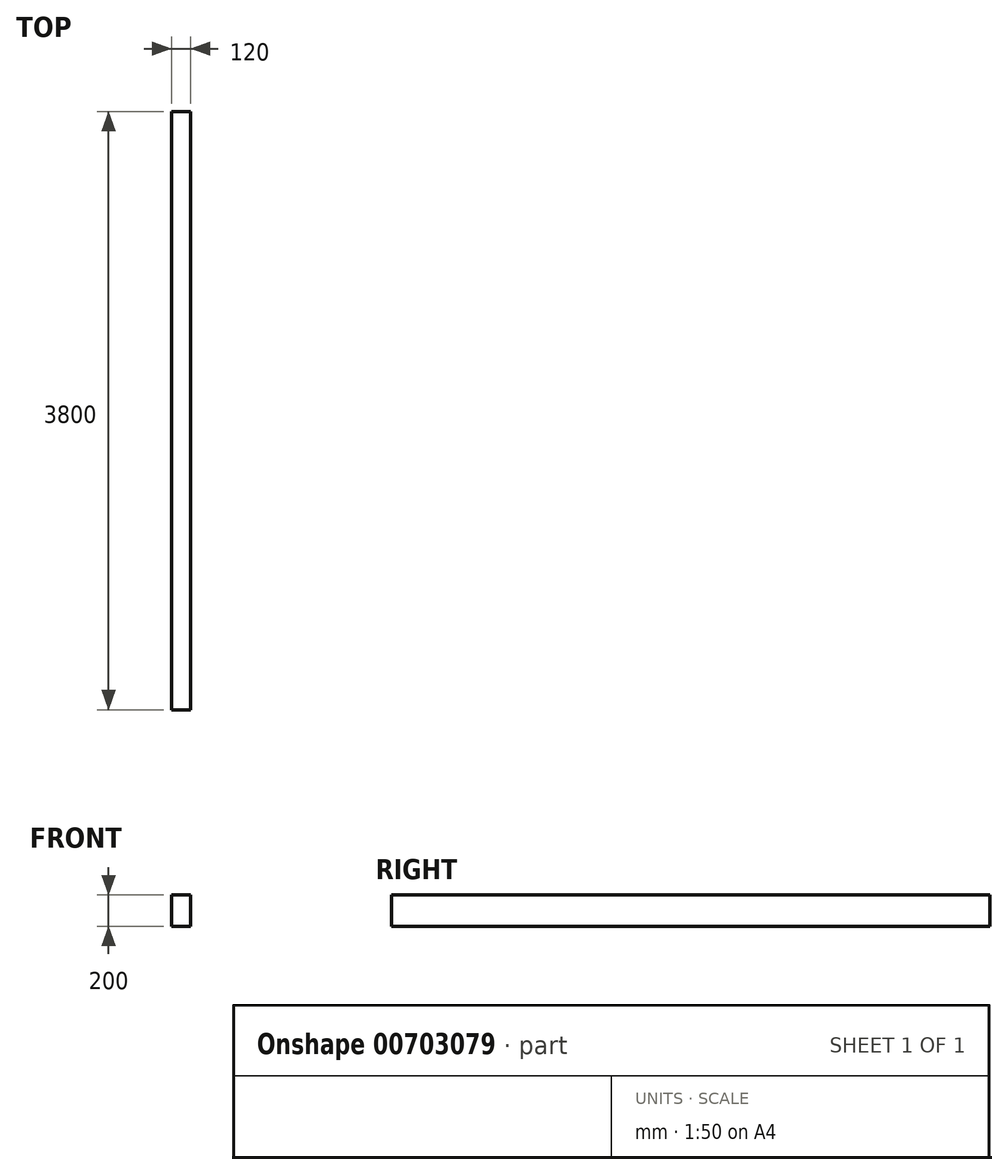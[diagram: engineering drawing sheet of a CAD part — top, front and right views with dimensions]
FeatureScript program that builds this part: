
annotation { "Feature Type Name" : "Feature", "Feature Type Description" : "" }
export const myFeature = defineFeature(function(context is Context, id is Id, definition is map)
    precondition{}
    {
        {
            var Q0;
            Q0=qCreatedBy(makeId("Front.planeOp"),FACE);
            var sketch = newSketch(context, id + "F0", { "sketchPlane" : qUnion([Q0])});
            skLineSegment(sketch, "E0.bottom", {"start": v(-59.35, 125.84) * mm, "end": v(60.65, 125.84) * mm});
            skLineSegment(sketch, "E0.top", {"start": v(-59.35, -74.16) * mm, "end": v(60.65, -74.16) * mm});
            skLineSegment(sketch, "E0.left", {"start": v(-59.35, 125.84) * mm, "end": v(-59.35, -74.16) * mm});
            skLineSegment(sketch, "E0.right", {"start": v(60.65, 125.84) * mm, "end": v(60.65, -74.16) * mm});
            skSolve(sketch);
        }
        {
            var Q0;
            Q0=makeQuery(id+"F0.imprint","IMPRINT",FACE,{"disambiguationData":[TD([[makeQuery(id+"F0.imprint","IMPRINT",EDGE,{"derivedFrom":sQuery(id+"F0.wireOp",EDGE,"E0.bottom")}),-1.0]])]});
            extrude(context, id + "F1", {"entities" : qUnion([Q0]), "depth" : 3800 * mm, "offsetDistance" : 25 * mm});
        }
    });
